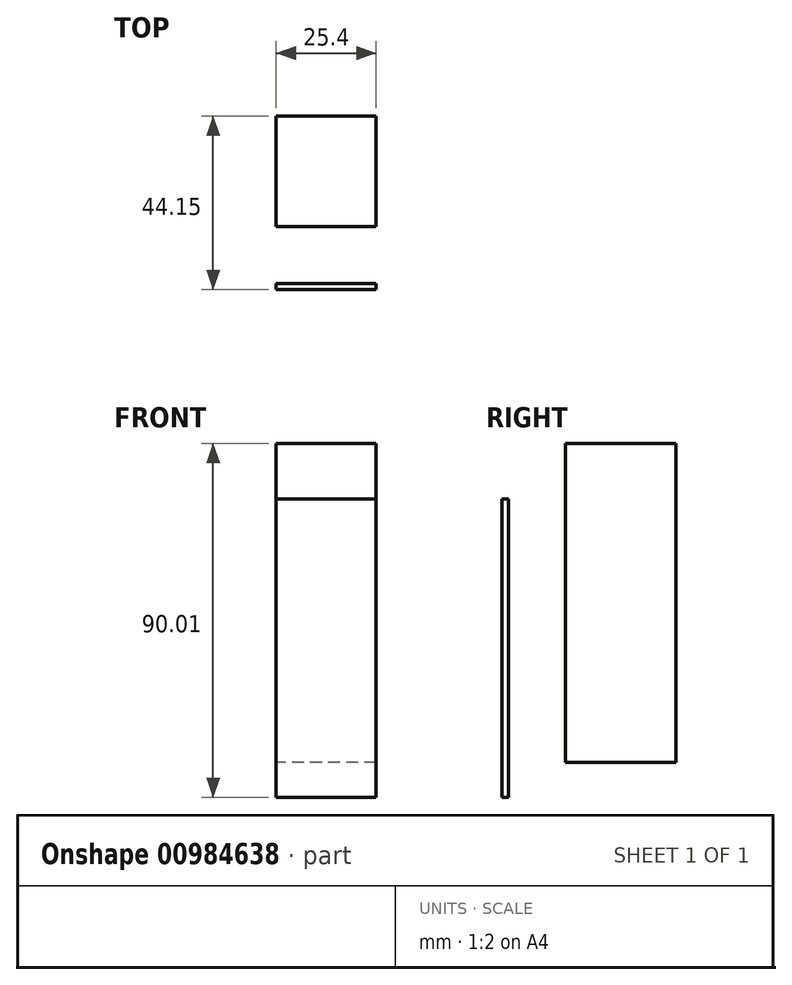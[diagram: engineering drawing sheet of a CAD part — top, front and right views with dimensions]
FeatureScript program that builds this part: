
annotation { "Feature Type Name" : "Feature", "Feature Type Description" : "" }
export const myFeature = defineFeature(function(context is Context, id is Id, definition is map)
    precondition{}
    {
        {
            var Q0;
            Q0=qCreatedBy(makeId("Right.planeOp"),FACE);
            var sketch = newSketch(context, id + "F0", { "sketchPlane" : qUnion([Q0])});
            skLineSegment(sketch, "E0.bottom", {"start": v(-9.62, 14.31) * mm, "end": v(-55.92, 14.31) * mm});
            skLineSegment(sketch, "E0.top", {"start": v(-9.62, -24.6) * mm, "end": v(-55.92, -24.6) * mm});
            skLineSegment(sketch, "E0.left", {"start": v(-9.62, 14.31) * mm, "end": v(-9.62, -24.6) * mm});
            skLineSegment(sketch, "E0.right", {"start": v(-55.92, 14.31) * mm, "end": v(-55.92, -24.6) * mm});
            skLineSegment(sketch, "E1.bottom", {"start": v(34.53, -15.66) * mm, "end": v(6.44, -15.66) * mm});
            skLineSegment(sketch, "E1.top", {"start": v(34.53, 65.41) * mm, "end": v(6.44, 65.41) * mm});
            skLineSegment(sketch, "E1.left", {"start": v(34.53, -15.66) * mm, "end": v(34.53, 65.41) * mm});
            skLineSegment(sketch, "E1.right", {"start": v(6.44, -15.66) * mm, "end": v(6.44, 65.41) * mm});
            skLineSegment(sketch, "E2.bottom", {"start": v(-7.98, 51.22) * mm, "end": v(-9.62, 51.22) * mm});
            skLineSegment(sketch, "E2.top", {"start": v(-7.98, -24.6) * mm, "end": v(-9.62, -24.6) * mm});
            skLineSegment(sketch, "E2.left", {"start": v(-7.98, 51.22) * mm, "end": v(-7.98, -24.6) * mm});
            skLineSegment(sketch, "E2.right", {"start": v(-9.62, 51.22) * mm, "end": v(-9.62, -24.6) * mm});
            skSolve(sketch);
        }
        {
            var Q0;
            {var subQ2=sQuery(id+"F0.wireOp",EDGE,"E2.bottom");Q0=makeQuery(id+"F0.imprint","IMPRINT",FACE,{"disambiguationData":[TD([[makeQuery(id+"F0.imprint","IMPRINT",EDGE,{"derivedFrom":subQ2}),1.0]])]});}
            var Q1;
            Q1=makeQuery(id+"F0.imprint","IMPRINT",FACE,{"disambiguationData":[TD([[makeQuery(id+"F0.imprint","IMPRINT",EDGE,{"derivedFrom":sQuery(id+"F0.wireOp",EDGE,"E1.bottom")}),-1.0]])]});
            extrude(context, id + "F1", {"entities" : qUnion([Q0, Q1]), "depth" : 25.4 * mm, "offsetDistance" : 25.4 * mm});
        }
    });
